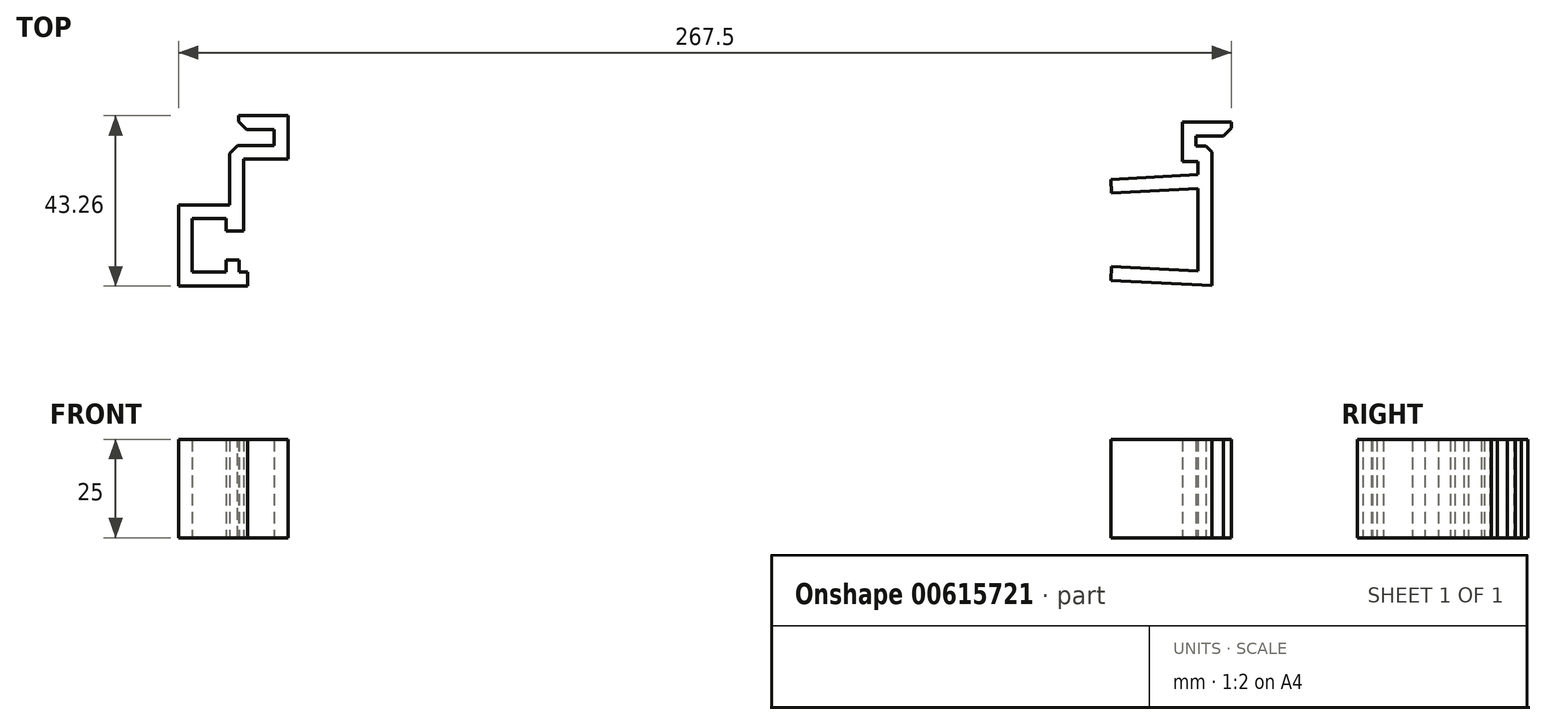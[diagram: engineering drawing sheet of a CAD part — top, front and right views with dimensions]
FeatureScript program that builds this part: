
annotation { "Feature Type Name" : "Feature", "Feature Type Description" : "" }
export const myFeature = defineFeature(function(context is Context, id is Id, definition is map)
    precondition{}
    {
        {
            var Q0;
            Q0=qCreatedBy(makeId("Top.planeOp"),FACE);
            var sketch = newSketch(context, id + "F0", { "sketchPlane" : qUnion([Q0])});
            skLineSegment(sketch, "E0", {"start": v(-134.35, 36.56) * mm, "end": v(144.92, 36.56) * mm});
            skLineSegment(sketch, "E1", {"start": v(-125.78, 20.56) * mm, "end": v(-102.78, 20.56) * mm});
            skLineSegment(sketch, "E2", {"start": v(-102.78, 15.82) * mm, "end": v(-113.28, 15.82) * mm});
            skLineSegment(sketch, "E3", {"start": v(-113.28, 15.82) * mm, "end": v(-113.28, 7.82) * mm});
            skLineSegment(sketch, "E4", {"start": v(-113.28, 7.82) * mm, "end": v(-102.78, 7.82) * mm});
            skLineSegment(sketch, "E5", {"start": v(-125.78, 5.76) * mm, "end": v(-125.78, 20.56) * mm});
            skLineSegment(sketch, "E6", {"start": v(144.92, 36.56) * mm, "end": v(144.92, 5.16) * mm});
            skLineSegment(sketch, "E7", {"start": v(144.92, 5.16) * mm, "end": v(131.92, 5.16) * mm});
            skLineSegment(sketch, "E8", {"start": v(131.92, 5.16) * mm, "end": v(131.92, 6.56) * mm});
            skLineSegment(sketch, "E9", {"start": v(131.92, 6.56) * mm, "end": v(142.92, 6.56) * mm});
            skLineSegment(sketch, "E10", {"start": v(142.92, 6.56) * mm, "end": v(142.92, 27.56) * mm});
            skLineSegment(sketch, "E11", {"start": v(142.92, 27.56) * mm, "end": v(119.92, 27.56) * mm});
            skLineSegment(sketch, "E12", {"start": v(119.92, 27.56) * mm, "end": v(119.92, 36.56) * mm});
            skLineSegment(sketch, "E13", {"start": v(-97.78, -7.34) * mm, "end": v(-109.78, -7.34) * mm});
            skLineSegment(sketch, "E14", {"start": v(-109.78, -7.34) * mm, "end": v(-109.78, -17.14) * mm});
            skLineSegment(sketch, "E15", {"start": v(-109.78, -17.14) * mm, "end": v(-114.78, -17.14) * mm});
            skLineSegment(sketch, "E16", {"start": v(-114.78, -17.14) * mm, "end": v(-114.78, -14.14) * mm});
            skLineSegment(sketch, "E17", {"start": v(-114.78, -14.14) * mm, "end": v(-122.78, -14.14) * mm});
            skLineSegment(sketch, "E18", {"start": v(-122.78, -14.14) * mm, "end": v(-122.78, -27.14) * mm});
            skLineSegment(sketch, "E19", {"start": v(-122.78, -27.14) * mm, "end": v(-114.78, -27.14) * mm});
            skLineSegment(sketch, "E20", {"start": v(-114.78, -27.14) * mm, "end": v(-114.78, -24.14) * mm});
            skLineSegment(sketch, "E21", {"start": v(-114.78, -24.14) * mm, "end": v(-111.03, -24.14) * mm});
            skLineSegment(sketch, "E22", {"start": v(-111.03, -24.14) * mm, "end": v(-111.03, -27.14) * mm});
            skLineSegment(sketch, "E23", {"start": v(-111.03, -27.14) * mm, "end": v(-108.53, -27.14) * mm});
            skLineSegment(sketch, "E24", {"start": v(-108.53, -27.14) * mm, "end": v(-108.53, -32.14) * mm});
            skLineSegment(sketch, "E25", {"start": v(-108.53, -32.14) * mm, "end": v(-97.78, -32.14) * mm});
            skLineSegment(sketch, "E26", {"start": v(110.45, -7.34) * mm, "end": v(132.42, -6.2) * mm});
            skLineSegment(sketch, "E27", {"start": v(132.42, -6.2) * mm, "end": v(132.42, -27.2) * mm});
            skLineSegment(sketch, "E28", {"start": v(132.42, -27.2) * mm, "end": v(110.45, -26.04) * mm});
            skLineSegment(sketch, "E29", {"start": v(110.45, -26.04) * mm, "end": v(110.45, -7.34) * mm});
            skLineSegment(sketch, "E30", {"start": v(128.42, 10.66) * mm, "end": v(140.92, 10.66) * mm});
            skLineSegment(sketch, "E31", {"start": v(140.92, 10.66) * mm, "end": v(140.92, 7.16) * mm});
            skLineSegment(sketch, "E32", {"start": v(140.92, 7.16) * mm, "end": v(131.92, 7.16) * mm});
            skLineSegment(sketch, "E33", {"start": v(135.92, 4.56) * mm, "end": v(135.92, -30.88) * mm});
            skLineSegment(sketch, "E34", {"start": v(132.42, -6.2) * mm, "end": v(135.92, -6.2) * mm, "construction": true});
            skLineSegment(sketch, "E35", {"start": v(-110.08, -16.94) * mm, "end": v(-114.48, -16.94) * mm});
            skLineSegment(sketch, "E36", {"start": v(-114.48, -16.94) * mm, "end": v(-114.48, -13.84) * mm});
            skLineSegment(sketch, "E37", {"start": v(-114.48, -13.84) * mm, "end": v(-123.08, -13.84) * mm});
            skLineSegment(sketch, "E38", {"start": v(-123.08, -13.84) * mm, "end": v(-123.08, -27.44) * mm});
            skLineSegment(sketch, "E39", {"start": v(-123.08, -27.44) * mm, "end": v(-114.48, -27.44) * mm});
            skLineSegment(sketch, "E40", {"start": v(-114.48, -27.44) * mm, "end": v(-114.48, -24.34) * mm});
            skLineSegment(sketch, "E41", {"start": v(-126.58, -30.94) * mm, "end": v(-126.58, -10.34) * mm});
            skLineSegment(sketch, "E42", {"start": v(-126.58, -10.34) * mm, "end": v(-113.58, -10.34) * mm});
            skLineSegment(sketch, "E43", {"start": v(-109.78, -16.94) * mm, "end": v(-110.08, -16.94) * mm, "construction": true});
            skLineSegment(sketch, "E44", {"start": v(-114.48, -16.94) * mm, "end": v(-114.78, -16.94) * mm, "construction": true});
            skLineSegment(sketch, "E45", {"start": v(-114.78, -14.14) * mm, "end": v(-114.78, -13.84) * mm, "construction": true});
            skLineSegment(sketch, "E46", {"start": v(-122.78, -14.14) * mm, "end": v(-123.08, -14.14) * mm, "construction": true});
            skLineSegment(sketch, "E47", {"start": v(-121.96, -27.14) * mm, "end": v(-121.96, -27.44) * mm, "construction": true});
            skLineSegment(sketch, "E48", {"start": v(-114.48, -24.34) * mm, "end": v(-114.78, -24.34) * mm, "construction": true});
            skLineSegment(sketch, "E49", {"start": v(-114.48, -24.34) * mm, "end": v(-111.23, -24.34) * mm});
            skLineSegment(sketch, "E50", {"start": v(-111.23, -24.34) * mm, "end": v(-111.23, -27.44) * mm});
            skLineSegment(sketch, "E51", {"start": v(-111.23, -27.44) * mm, "end": v(-109.03, -27.44) * mm});
            skLineSegment(sketch, "E52", {"start": v(-109.03, -27.44) * mm, "end": v(-109.03, -30.94) * mm});
            skLineSegment(sketch, "E53", {"start": v(-109.03, -30.94) * mm, "end": v(-126.58, -30.94) * mm});
            skLineSegment(sketch, "E54", {"start": v(132.42, -2.7) * mm, "end": v(110.27, -3.85) * mm});
            skLineSegment(sketch, "E55", {"start": v(110.27, -3.85) * mm, "end": v(110.45, -7.34) * mm});
            skLineSegment(sketch, "E56", {"start": v(135.92, -30.88) * mm, "end": v(110.27, -29.54) * mm});
            skLineSegment(sketch, "E57", {"start": v(110.27, -29.54) * mm, "end": v(110.45, -26.04) * mm});
            skLineSegment(sketch, "E58", {"start": v(-97.78, -7.34) * mm, "end": v(110.45, -7.34) * mm, "construction": true});
            skLineSegment(sketch, "E59", {"start": v(131.92, 4.56) * mm, "end": v(135.92, 4.56) * mm});
            skLineSegment(sketch, "E60", {"start": v(131.92, 6.56) * mm, "end": v(131.92, 7.16) * mm});
            skLineSegment(sketch, "E61", {"start": v(131.92, 5.16) * mm, "end": v(131.92, 4.56) * mm});
            skLineSegment(sketch, "E62", {"start": v(128.42, 10.66) * mm, "end": v(128.42, 0.62) * mm});
            skLineSegment(sketch, "E63", {"start": v(128.42, 0.62) * mm, "end": v(132.42, 0.62) * mm});
            skLineSegment(sketch, "E64", {"start": v(132.42, 0.62) * mm, "end": v(132.42, -2.7) * mm});
            skLineSegment(sketch, "E65", {"start": v(-125.78, 5.76) * mm, "end": v(-102.78, 5.76) * mm});
            skLineSegment(sketch, "E66", {"start": v(-102.78, 5.76) * mm, "end": v(-102.78, 7.82) * mm});
            skLineSegment(sketch, "E67", {"start": v(-102.78, 20.56) * mm, "end": v(-102.78, 15.82) * mm});
            skLineSegment(sketch, "E68", {"start": v(-110.08, -16.94) * mm, "end": v(-110.08, 1.26) * mm});
            skLineSegment(sketch, "E69", {"start": v(-110.08, 1.26) * mm, "end": v(-98.78, 1.26) * mm});
            skLineSegment(sketch, "E70", {"start": v(-98.78, 1.26) * mm, "end": v(-98.78, 12.32) * mm});
            skLineSegment(sketch, "E71", {"start": v(-98.78, 12.32) * mm, "end": v(-111.28, 12.32) * mm});
            skLineSegment(sketch, "E72", {"start": v(-111.28, 12.32) * mm, "end": v(-111.28, 8.82) * mm});
            skLineSegment(sketch, "E73", {"start": v(-111.28, 8.82) * mm, "end": v(-102.28, 8.82) * mm});
            skLineSegment(sketch, "E74", {"start": v(-102.28, 8.82) * mm, "end": v(-102.28, 4.76) * mm});
            skLineSegment(sketch, "E75", {"start": v(-102.28, 4.76) * mm, "end": v(-113.58, 4.76) * mm});
            skLineSegment(sketch, "E76", {"start": v(-113.58, 4.76) * mm, "end": v(-113.58, -10.34) * mm});
            skLineSegment(sketch, "E77", {"start": v(-97.78, 0) * mm, "end": v(-97.78, -7.34) * mm});
            skSolve(sketch);
        }
        {
            var Q0;
            Q0=makeQuery(id+"F0.imprint","IMPRINT",FACE,{"disambiguationData":[TD([[makeQuery(id+"F0.imprint","IMPRINT",EDGE,{"derivedFrom":sQuery(id+"F0.wireOp",EDGE,"E8")}),1.0]])]});
            var Q1;
            Q1=makeQuery(id+"F0.imprint","IMPRINT",FACE,{"disambiguationData":[TD([[makeQuery(id+"F0.imprint","IMPRINT",EDGE,{"derivedFrom":sQuery(id+"F0.wireOp",EDGE,"E35")}),-1.0]])]});
            extrude(context, id + "F1", {"entities" : qUnion([Q0, Q1]), "depth" : 25 * mm, "offsetDistance" : 25 * mm});
        }
        {
            var Q0;
            Q0=makeQuery(id+"F1.opExtrude","SWEPT_EDGE",EDGE,{"disambiguationData":[OSD([sQuery(id+"F0.wireOp",EDGE,"E31"),sQuery(id+"F0.wireOp",EDGE,"E32")])]});
            var Q1;
            Q1=makeQuery(id+"F1.opExtrude","SWEPT_EDGE",EDGE,{"disambiguationData":[OSD([sQuery(id+"F0.wireOp",EDGE,"E72"),sQuery(id+"F0.wireOp",EDGE,"E73")])]});
            var Q2;
            Q2=makeQuery(id+"F1.opExtrude","SWEPT_EDGE",EDGE,{"disambiguationData":[OSD([sQuery(id+"F0.wireOp",EDGE,"E75"),sQuery(id+"F0.wireOp",EDGE,"E76")])]});
            chamfer(context, id + "F2", {"entities" : qUnion([Q0, Q1, Q2]), "width" : 2 * mm, "tangentPropagation" : true});
        }
        {
            var Q0;
            Q0=makeQuery(id+"F1.opExtrude","SWEPT_EDGE",EDGE,{"disambiguationData":[OSD([sQuery(id+"F0.wireOp",EDGE,"E33"),sQuery(id+"F0.wireOp",EDGE,"E59")])]});
            chamfer(context, id + "F3", {"entities" : qUnion([Q0]), "width" : 1.5 * mm, "tangentPropagation" : true});
        }
    });
